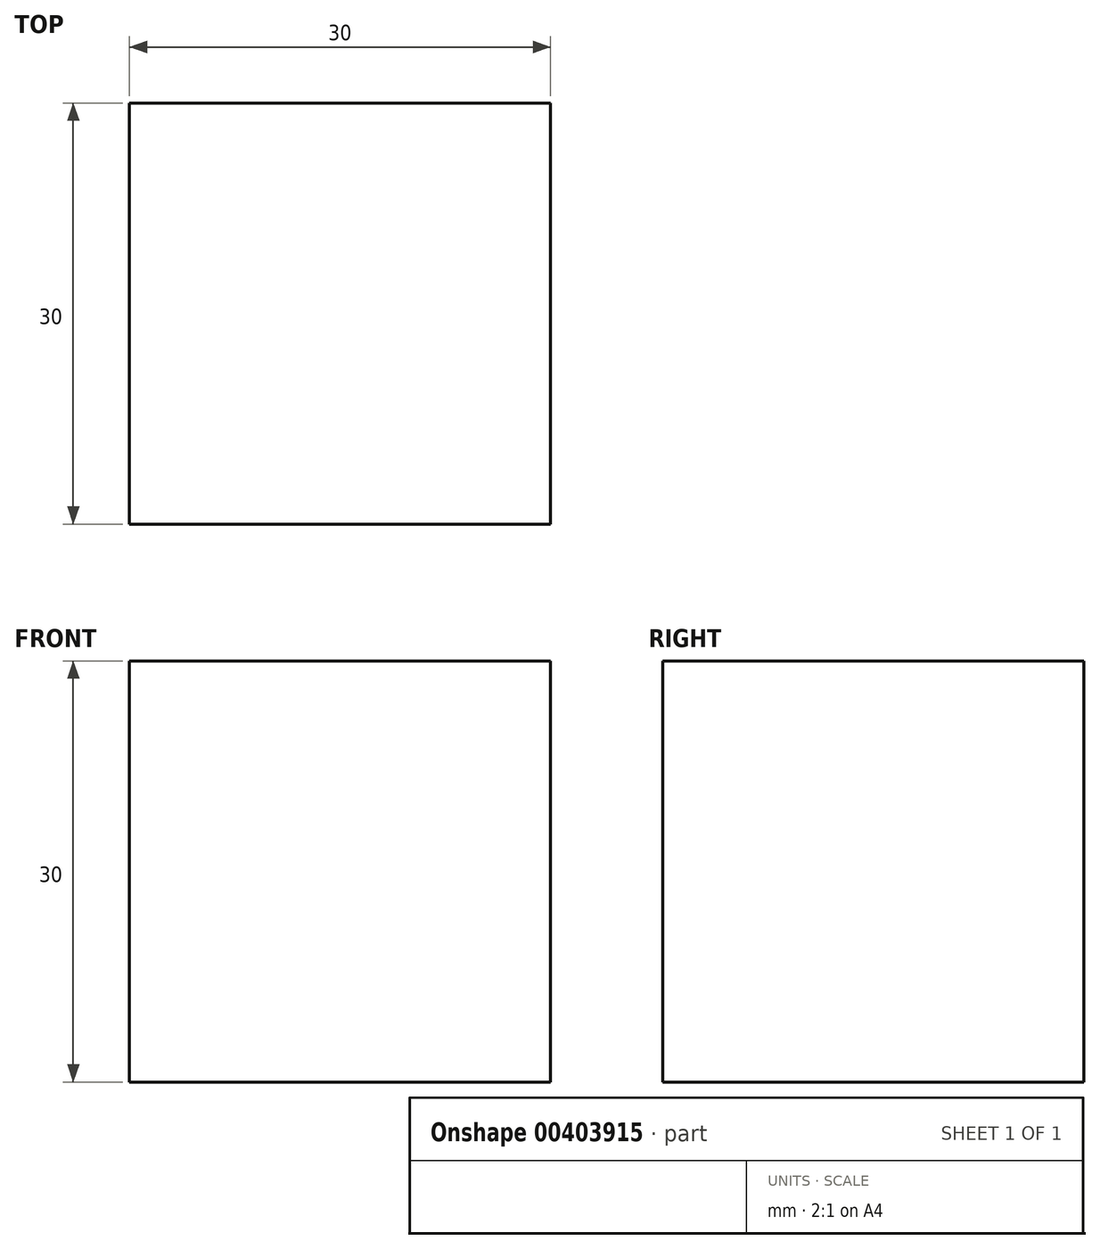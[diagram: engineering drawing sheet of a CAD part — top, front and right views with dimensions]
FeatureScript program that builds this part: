
annotation { "Feature Type Name" : "Feature", "Feature Type Description" : "" }
export const myFeature = defineFeature(function(context is Context, id is Id, definition is map)
    precondition{}
    {
        {
            var Q0;
            Q0=qCreatedBy(makeId("Top.planeOp"),FACE);
            var sketch = newSketch(context, id + "F0", { "sketchPlane" : qUnion([Q0])});
            skLineSegment(sketch, "E0.bottom", {"start": v(15, 15) * mm, "end": v(-15, 15) * mm});
            skLineSegment(sketch, "E0.top", {"start": v(15, -15) * mm, "end": v(-15, -15) * mm});
            skLineSegment(sketch, "E0.left", {"start": v(15, 15) * mm, "end": v(15, -15) * mm});
            skLineSegment(sketch, "E0.right", {"start": v(-15, 15) * mm, "end": v(-15, -15) * mm});
            skPoint(sketch, "E0.middle", {"position": v(0, 0) * mm});
            skSolve(sketch);
        }
        {
            var Q0;
            Q0 = qSketchRegion(id + "F0", true);
            extrude(context, id + "F1", {"entities" : qUnion([Q0]), "depth" : 30 * mm});
        }
    });
